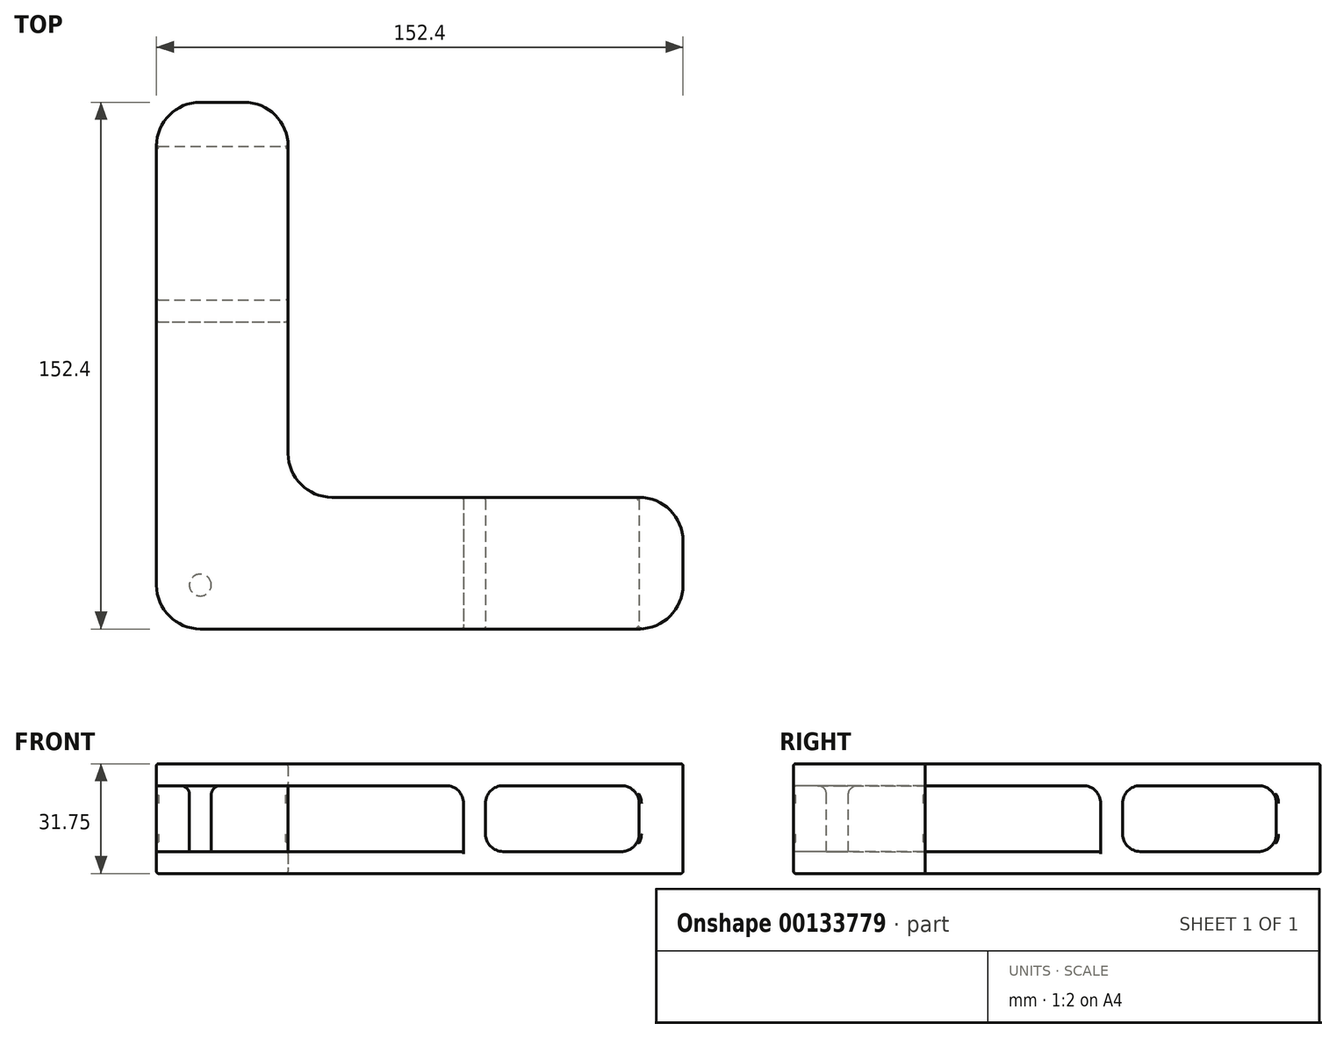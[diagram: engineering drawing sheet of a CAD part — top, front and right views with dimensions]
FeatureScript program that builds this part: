
annotation { "Feature Type Name" : "Feature", "Feature Type Description" : "" }
export const myFeature = defineFeature(function(context is Context, id is Id, definition is map)
    precondition{}
    {
        {
            var Q0;
            Q0=qCreatedBy(makeId("Top.planeOp"),FACE);
            var sketch = newSketch(context, id + "F0", { "sketchPlane" : qUnion([Q0])});
            skLineSegment(sketch, "E0", {"start": v(0, 12.7) * mm, "end": v(0, 139.7) * mm});
            skLineSegment(sketch, "E1", {"start": v(12.7, 152.4) * mm, "end": v(25.4, 152.4) * mm});
            skLineSegment(sketch, "E2", {"start": v(38.1, 139.7) * mm, "end": v(38.1, 50.8) * mm});
            skLineSegment(sketch, "E3", {"start": v(50.8, 38.1) * mm, "end": v(139.7, 38.1) * mm});
            skLineSegment(sketch, "E4", {"start": v(152.4, 25.4) * mm, "end": v(152.4, 12.7) * mm});
            skLineSegment(sketch, "E5", {"start": v(139.7, 0) * mm, "end": v(12.7, 0) * mm});
            skPoint(sketch, "E6.visualSharp", {"position": v(0, 0) * mm});
            skArc(sketch, "E6.filletArc", {"start": v(0, 12.7) * mm, "mid": v(3.72, 3.72) * mm, "end": v(12.7, 0) * mm});
            skPoint(sketch, "E7.visualSharp", {"position": v(0, 152.4) * mm});
            skArc(sketch, "E7.filletArc", {"start": v(12.7, 152.4) * mm, "mid": v(3.72, 148.68) * mm, "end": v(0, 139.7) * mm});
            skPoint(sketch, "E8.visualSharp", {"position": v(38.1, 152.4) * mm});
            skArc(sketch, "E8.filletArc", {"start": v(38.1, 139.7) * mm, "mid": v(34.38, 148.68) * mm, "end": v(25.4, 152.4) * mm});
            skPoint(sketch, "E9.visualSharp", {"position": v(38.1, 38.1) * mm});
            skArc(sketch, "E9.filletArc", {"start": v(38.1, 50.8) * mm, "mid": v(41.82, 41.82) * mm, "end": v(50.8, 38.1) * mm});
            skPoint(sketch, "E10.visualSharp", {"position": v(152.4, 38.1) * mm});
            skArc(sketch, "E10.filletArc", {"start": v(152.4, 25.4) * mm, "mid": v(148.68, 34.38) * mm, "end": v(139.7, 38.1) * mm});
            skPoint(sketch, "E11.visualSharp", {"position": v(152.4, 0) * mm});
            skArc(sketch, "E11.filletArc", {"start": v(139.7, 0) * mm, "mid": v(148.68, 3.72) * mm, "end": v(152.4, 12.7) * mm});
            skSolve(sketch);
        }
        {
            var Q0;
            Q0=makeQuery(id+"F0.imprint","IMPRINT",FACE,{"disambiguationData":[TD([[makeQuery(id+"F0.imprint","IMPRINT",EDGE,{"derivedFrom":sQuery(id+"F0.wireOp",EDGE,"E0")}),-1.0]])]});
            extrude(context, id + "F1", {"entities" : qUnion([Q0]), "depth" : 6.35 * mm});
        }
        {
            var Q0;
            Q0=makeQuery(id+"F1.opExtrude","CAP_FACE",FACE,{"disambiguationData":[OSD([sQuery(id+"F0.wireOp",EDGE,"E0"),sQuery(id+"F0.wireOp",EDGE,"E1"),sQuery(id+"F0.wireOp",EDGE,"E2"),sQuery(id+"F0.wireOp",EDGE,"E3"),sQuery(id+"F0.wireOp",EDGE,"E4"),sQuery(id+"F0.wireOp",EDGE,"E5"),sQuery(id+"F0.wireOp",EDGE,"E6.filletArc"),sQuery(id+"F0.wireOp",EDGE,"E7.filletArc"),sQuery(id+"F0.wireOp",EDGE,"E8.filletArc"),sQuery(id+"F0.wireOp",EDGE,"E9.filletArc"),sQuery(id+"F0.wireOp",EDGE,"E10.filletArc"),sQuery(id+"F0.wireOp",EDGE,"E11.filletArc")])],"isStart":false});
            extrude(context, id + "F2", {"entities" : qUnion([Q0]), "depth" : 6.35 * mm});
        }
        {
            var Q0;
            Q0=makeQuery(id+"F2.opExtrude","SWEPT_BODY",BODY,{"disambiguationData":[OSD([sQuery(id+"F0.wireOp",EDGE,"E0"),sQuery(id+"F0.wireOp",EDGE,"E1"),sQuery(id+"F0.wireOp",EDGE,"E2"),sQuery(id+"F0.wireOp",EDGE,"E3"),sQuery(id+"F0.wireOp",EDGE,"E4"),sQuery(id+"F0.wireOp",EDGE,"E5"),sQuery(id+"F0.wireOp",EDGE,"E6.filletArc"),sQuery(id+"F0.wireOp",EDGE,"E7.filletArc"),sQuery(id+"F0.wireOp",EDGE,"E8.filletArc"),sQuery(id+"F0.wireOp",EDGE,"E9.filletArc"),sQuery(id+"F0.wireOp",EDGE,"E10.filletArc"),sQuery(id+"F0.wireOp",EDGE,"E11.filletArc")])]});
            transform(context, id + "F3", {"entities" : qUnion([Q0]), "transformType" : TransformType.TRANSLATION_3D, "dx" : 0 * mm, "dy" : 0 * mm, "dz" : 19.05 * mm, "makeCopy" : false});
        }
        {
            var Q0;
            Q0=makeQuery(id+"F2.opExtrude","CAP_FACE",FACE,{"disambiguationData":[OSD([sQuery(id+"F0.wireOp",EDGE,"E0"),sQuery(id+"F0.wireOp",EDGE,"E1"),sQuery(id+"F0.wireOp",EDGE,"E2"),sQuery(id+"F0.wireOp",EDGE,"E3"),sQuery(id+"F0.wireOp",EDGE,"E4"),sQuery(id+"F0.wireOp",EDGE,"E5"),sQuery(id+"F0.wireOp",EDGE,"E6.filletArc"),sQuery(id+"F0.wireOp",EDGE,"E7.filletArc"),sQuery(id+"F0.wireOp",EDGE,"E8.filletArc"),sQuery(id+"F0.wireOp",EDGE,"E9.filletArc"),sQuery(id+"F0.wireOp",EDGE,"E10.filletArc"),sQuery(id+"F0.wireOp",EDGE,"E11.filletArc")])],"isStart":false});
            var sketch = newSketch(context, id + "F4", { "sketchPlane" : qUnion([Q0])});
            skArc(sketch, "E12.0", {"start": v(38.1, 139.7) * mm, "mid": v(34.38, 148.68) * mm, "end": v(25.4, 152.4) * mm});
            skLineSegment(sketch, "E13.0", {"start": v(12.7, 152.4) * mm, "end": v(25.4, 152.4) * mm});
            skArc(sketch, "E14.0", {"start": v(12.7, 152.4) * mm, "mid": v(3.72, 148.68) * mm, "end": v(0, 139.7) * mm});
            skArc(sketch, "E15.0", {"start": v(152.4, 25.4) * mm, "mid": v(148.68, 34.38) * mm, "end": v(139.7, 38.1) * mm});
            skLineSegment(sketch, "E16.0", {"start": v(152.4, 25.4) * mm, "end": v(152.4, 12.7) * mm});
            skArc(sketch, "E17.0", {"start": v(139.7, 0) * mm, "mid": v(148.68, 3.72) * mm, "end": v(152.4, 12.7) * mm});
            skLineSegment(sketch, "E18.0", {"start": v(50.8, 38.1) * mm, "end": v(139.7, 38.1) * mm});
            skLineSegment(sketch, "E19.0", {"start": v(139.7, 0) * mm, "end": v(12.7, 0) * mm});
            skLineSegment(sketch, "E20.0", {"start": v(38.1, 139.7) * mm, "end": v(38.1, 50.8) * mm});
            skLineSegment(sketch, "E21.0", {"start": v(0, 12.7) * mm, "end": v(0, 139.7) * mm});
            skArc(sketch, "E22.0", {"start": v(38.1, 50.8) * mm, "mid": v(41.82, 41.82) * mm, "end": v(50.8, 38.1) * mm});
            skArc(sketch, "E23.0", {"start": v(0, 12.7) * mm, "mid": v(3.72, 3.72) * mm, "end": v(12.7, 0) * mm});
            skLineSegment(sketch, "E24", {"start": v(0, 88.9) * mm, "end": v(38.1, 88.9) * mm});
            skLineSegment(sketch, "E25", {"start": v(88.9, 38.1) * mm, "end": v(88.9, 0) * mm});
            skLineSegment(sketch, "E26", {"start": v(95.25, 38.1) * mm, "end": v(95.25, 0) * mm});
            skLineSegment(sketch, "E27", {"start": v(0, 95.25) * mm, "end": v(38.1, 95.25) * mm});
            skLineSegment(sketch, "E28", {"start": v(0, 139.7) * mm, "end": v(38.1, 139.7) * mm});
            skLineSegment(sketch, "E29", {"start": v(139.7, 38.1) * mm, "end": v(139.7, 0) * mm});
            skSolve(sketch);
        }
        {
            var Q0;
            {var subQ0=sQuery(id+"F4.wireOp",EDGE,"E24");Q0=makeQuery(id+"F4.imprint","IMPRINT",FACE,{"disambiguationData":[TD([[makeQuery(id+"F4.imprint","IMPRINT",EDGE,{"derivedFrom":subQ0}),1.0]])]});}
            var Q1;
            Q1=makeQuery(id+"F4.imprint","IMPRINT",FACE,{"disambiguationData":[TD([[makeQuery(id+"F4.imprint","IMPRINT",EDGE,{"derivedFrom":sQuery(id+"F4.wireOp",EDGE,"E14.0")}),1.0]])]});
            var Q2;
            Q2=makeQuery(id+"F4.imprint","IMPRINT",FACE,{"disambiguationData":[TD([[makeQuery(id+"F4.imprint","IMPRINT",EDGE,{"derivedFrom":sQuery(id+"F4.wireOp",EDGE,"E15.0")}),1.0]])]});
            var Q3;
            {var subQ0=sQuery(id+"F4.wireOp",EDGE,"E25");Q3=makeQuery(id+"F4.imprint","IMPRINT",FACE,{"disambiguationData":[TD([[makeQuery(id+"F4.imprint","IMPRINT",EDGE,{"derivedFrom":subQ0}),1.0]])]});}
            extrude(context, id + "F5", {"entities" : qUnion([Q0, Q1, Q2, Q3]), "operationType" : NewBodyOperationType.ADD, "oppositeDirection" : true, "depth" : 25.4 * mm});
        }
        {
            var Q0;
            Q0=makeQuery(id+"F5.opExtrude","CAP_EDGE",EDGE,{"disambiguationData":[OSD([sQuery(id+"F4.wireOp",EDGE,"E28")])],"isStart":false});
            var Q1;
            Q1=makeQuery(id+"F5.boolean.opBoolean","INTERSECT",EDGE,{"derivedFrom":[makeQuery(id+"F2.opExtrude","CAP_FACE",FACE,{"disambiguationData":[OSD([sQuery(id+"F0.wireOp",EDGE,"E0"),sQuery(id+"F0.wireOp",EDGE,"E1"),sQuery(id+"F0.wireOp",EDGE,"E2"),sQuery(id+"F0.wireOp",EDGE,"E3"),sQuery(id+"F0.wireOp",EDGE,"E4"),sQuery(id+"F0.wireOp",EDGE,"E5"),sQuery(id+"F0.wireOp",EDGE,"E6.filletArc"),sQuery(id+"F0.wireOp",EDGE,"E7.filletArc"),sQuery(id+"F0.wireOp",EDGE,"E8.filletArc"),sQuery(id+"F0.wireOp",EDGE,"E9.filletArc"),sQuery(id+"F0.wireOp",EDGE,"E10.filletArc"),sQuery(id+"F0.wireOp",EDGE,"E11.filletArc")])],"isStart":true}),makeQuery(id+"F5.opExtrude","SWEPT_FACE",FACE,{"disambiguationData":[OSD([sQuery(id+"F4.wireOp",EDGE,"E28")])]})]});
            var Q2;
            Q2=makeQuery(id+"F5.boolean.opBoolean","INTERSECT",EDGE,{"derivedFrom":[makeQuery(id+"F2.opExtrude","CAP_FACE",FACE,{"disambiguationData":[OSD([sQuery(id+"F0.wireOp",EDGE,"E0"),sQuery(id+"F0.wireOp",EDGE,"E1"),sQuery(id+"F0.wireOp",EDGE,"E2"),sQuery(id+"F0.wireOp",EDGE,"E3"),sQuery(id+"F0.wireOp",EDGE,"E4"),sQuery(id+"F0.wireOp",EDGE,"E5"),sQuery(id+"F0.wireOp",EDGE,"E6.filletArc"),sQuery(id+"F0.wireOp",EDGE,"E7.filletArc"),sQuery(id+"F0.wireOp",EDGE,"E8.filletArc"),sQuery(id+"F0.wireOp",EDGE,"E9.filletArc"),sQuery(id+"F0.wireOp",EDGE,"E10.filletArc"),sQuery(id+"F0.wireOp",EDGE,"E11.filletArc")])],"isStart":true}),makeQuery(id+"F5.opExtrude","SWEPT_FACE",FACE,{"disambiguationData":[OSD([sQuery(id+"F4.wireOp",EDGE,"E27")])]})]});
            var Q3;
            Q3=makeQuery(id+"F5.opExtrude","CAP_EDGE",EDGE,{"disambiguationData":[OSD([sQuery(id+"F4.wireOp",EDGE,"E27")])],"isStart":false});
            var Q4;
            Q4=makeQuery(id+"F5.boolean.opBoolean","INTERSECT",EDGE,{"derivedFrom":[makeQuery(id+"F2.opExtrude","CAP_FACE",FACE,{"disambiguationData":[OSD([sQuery(id+"F0.wireOp",EDGE,"E0"),sQuery(id+"F0.wireOp",EDGE,"E1"),sQuery(id+"F0.wireOp",EDGE,"E2"),sQuery(id+"F0.wireOp",EDGE,"E3"),sQuery(id+"F0.wireOp",EDGE,"E4"),sQuery(id+"F0.wireOp",EDGE,"E5"),sQuery(id+"F0.wireOp",EDGE,"E6.filletArc"),sQuery(id+"F0.wireOp",EDGE,"E7.filletArc"),sQuery(id+"F0.wireOp",EDGE,"E8.filletArc"),sQuery(id+"F0.wireOp",EDGE,"E9.filletArc"),sQuery(id+"F0.wireOp",EDGE,"E10.filletArc"),sQuery(id+"F0.wireOp",EDGE,"E11.filletArc")])],"isStart":true}),makeQuery(id+"F5.opExtrude","SWEPT_FACE",FACE,{"disambiguationData":[OSD([sQuery(id+"F4.wireOp",EDGE,"E24")])]})]});
            var Q5;
            Q5=makeQuery(id+"F5.opExtrude","CAP_EDGE",EDGE,{"disambiguationData":[OSD([sQuery(id+"F4.wireOp",EDGE,"E24")])],"isStart":false});
            var Q6;
            Q6=makeQuery(id+"F5.opExtrude","CAP_EDGE",EDGE,{"disambiguationData":[OSD([sQuery(id+"F4.wireOp",EDGE,"E25")])],"isStart":false});
            var Q7;
            Q7=makeQuery(id+"F5.opExtrude","CAP_EDGE",EDGE,{"disambiguationData":[OSD([sQuery(id+"F4.wireOp",EDGE,"E29")])],"isStart":false});
            var Q8;
            Q8=makeQuery(id+"F5.boolean.opBoolean","INTERSECT",EDGE,{"derivedFrom":[makeQuery(id+"F2.opExtrude","CAP_FACE",FACE,{"disambiguationData":[OSD([sQuery(id+"F0.wireOp",EDGE,"E0"),sQuery(id+"F0.wireOp",EDGE,"E1"),sQuery(id+"F0.wireOp",EDGE,"E2"),sQuery(id+"F0.wireOp",EDGE,"E3"),sQuery(id+"F0.wireOp",EDGE,"E4"),sQuery(id+"F0.wireOp",EDGE,"E5"),sQuery(id+"F0.wireOp",EDGE,"E6.filletArc"),sQuery(id+"F0.wireOp",EDGE,"E7.filletArc"),sQuery(id+"F0.wireOp",EDGE,"E8.filletArc"),sQuery(id+"F0.wireOp",EDGE,"E9.filletArc"),sQuery(id+"F0.wireOp",EDGE,"E10.filletArc"),sQuery(id+"F0.wireOp",EDGE,"E11.filletArc")])],"isStart":true}),makeQuery(id+"F5.opExtrude","SWEPT_FACE",FACE,{"disambiguationData":[OSD([sQuery(id+"F4.wireOp",EDGE,"E25")])]})]});
            var Q9;
            Q9=makeQuery(id+"F5.boolean.opBoolean","INTERSECT",EDGE,{"derivedFrom":[makeQuery(id+"F2.opExtrude","CAP_FACE",FACE,{"disambiguationData":[OSD([sQuery(id+"F0.wireOp",EDGE,"E0"),sQuery(id+"F0.wireOp",EDGE,"E1"),sQuery(id+"F0.wireOp",EDGE,"E2"),sQuery(id+"F0.wireOp",EDGE,"E3"),sQuery(id+"F0.wireOp",EDGE,"E4"),sQuery(id+"F0.wireOp",EDGE,"E5"),sQuery(id+"F0.wireOp",EDGE,"E6.filletArc"),sQuery(id+"F0.wireOp",EDGE,"E7.filletArc"),sQuery(id+"F0.wireOp",EDGE,"E8.filletArc"),sQuery(id+"F0.wireOp",EDGE,"E9.filletArc"),sQuery(id+"F0.wireOp",EDGE,"E10.filletArc"),sQuery(id+"F0.wireOp",EDGE,"E11.filletArc")])],"isStart":true}),makeQuery(id+"F5.opExtrude","SWEPT_FACE",FACE,{"disambiguationData":[OSD([sQuery(id+"F4.wireOp",EDGE,"E29")])]})]});
            var Q10;
            Q10=makeQuery(id+"F5.boolean.opBoolean","INTERSECT",EDGE,{"derivedFrom":[makeQuery(id+"F2.opExtrude","CAP_FACE",FACE,{"disambiguationData":[OSD([sQuery(id+"F0.wireOp",EDGE,"E0"),sQuery(id+"F0.wireOp",EDGE,"E1"),sQuery(id+"F0.wireOp",EDGE,"E2"),sQuery(id+"F0.wireOp",EDGE,"E3"),sQuery(id+"F0.wireOp",EDGE,"E4"),sQuery(id+"F0.wireOp",EDGE,"E5"),sQuery(id+"F0.wireOp",EDGE,"E6.filletArc"),sQuery(id+"F0.wireOp",EDGE,"E7.filletArc"),sQuery(id+"F0.wireOp",EDGE,"E8.filletArc"),sQuery(id+"F0.wireOp",EDGE,"E9.filletArc"),sQuery(id+"F0.wireOp",EDGE,"E10.filletArc"),sQuery(id+"F0.wireOp",EDGE,"E11.filletArc")])],"isStart":true}),makeQuery(id+"F5.opExtrude","SWEPT_FACE",FACE,{"disambiguationData":[OSD([sQuery(id+"F4.wireOp",EDGE,"E26")])]})]});
            var Q11;
            Q11=makeQuery(id+"F5.opExtrude","CAP_EDGE",EDGE,{"disambiguationData":[OSD([sQuery(id+"F4.wireOp",EDGE,"E26")])],"isStart":false});
            fillet(context, id + "F6", {"entities" : qUnion([Q0, Q1, Q2, Q3, Q4, Q5, Q6, Q7, Q8, Q9, Q10, Q11]), "radius" : 5.08 * mm, "tangentPropagation" : true, "allowEdgeOverflow" : false});
        }
        {
            var Q0;
            Q0=makeQuery(id+"F2.opExtrude","CAP_EDGE",EDGE,{"disambiguationData":[OSD([sQuery(id+"F0.wireOp",EDGE,"E0")])],"isStart":false});
            var Q1;
            Q1=makeQuery(id+"F1.opExtrude","CAP_EDGE",EDGE,{"disambiguationData":[OSD([sQuery(id+"F0.wireOp",EDGE,"E0")])],"isStart":true});
            var Q2;
            {var subQ0=sQuery(id+"F0.wireOp",EDGE,"E0");var subQ1=sQuery(id+"F0.wireOp",EDGE,"E7.filletArc");Q2=makeQuery(id+"F5.boolean.opBoolean","SPLIT",EDGE,{"disambiguationData":[TD([makeQuery(id+"F1.opExtrude","SWEPT_FACE",FACE,{"disambiguationData":[OSD([subQ1])]})])],"derivedFrom":makeQuery(id+"F1.opExtrude","CAP_EDGE",EDGE,{"disambiguationData":[OSD([subQ0])],"isStart":false})});}
            var Q3;
            {var subQ0=sQuery(id+"F0.wireOp",EDGE,"E0");var subQ1=sQuery(id+"F0.wireOp",EDGE,"E6.filletArc");Q3=makeQuery(id+"F5.boolean.opBoolean","SPLIT",EDGE,{"disambiguationData":[TD([makeQuery(id+"F1.opExtrude","SWEPT_FACE",FACE,{"disambiguationData":[OSD([subQ1])]})])],"derivedFrom":makeQuery(id+"F1.opExtrude","CAP_EDGE",EDGE,{"disambiguationData":[OSD([subQ0])],"isStart":false})});}
            var Q4;
            {var subQ0=sQuery(id+"F0.wireOp",EDGE,"E2");var subQ1=sQuery(id+"F0.wireOp",EDGE,"E8.filletArc");Q4=makeQuery(id+"F5.boolean.opBoolean","SPLIT",EDGE,{"disambiguationData":[TD([makeQuery(id+"F1.opExtrude","SWEPT_FACE",FACE,{"disambiguationData":[OSD([subQ1])]})])],"derivedFrom":makeQuery(id+"F2.opExtrude","CAP_EDGE",EDGE,{"disambiguationData":[OSD([subQ0])],"isStart":true})});}
            var Q5;
            {var subQ0=sQuery(id+"F0.wireOp",EDGE,"E2");var subQ1=sQuery(id+"F0.wireOp",EDGE,"E9.filletArc");Q5=makeQuery(id+"F5.boolean.opBoolean","SPLIT",EDGE,{"disambiguationData":[TD([makeQuery(id+"F1.opExtrude","SWEPT_FACE",FACE,{"disambiguationData":[OSD([subQ1])]})])],"derivedFrom":makeQuery(id+"F1.opExtrude","CAP_EDGE",EDGE,{"disambiguationData":[OSD([subQ0])],"isStart":false})});}
            var Q6;
            {var subQ0=sQuery(id+"F0.wireOp",EDGE,"E3");var subQ1=sQuery(id+"F0.wireOp",EDGE,"E10.filletArc");Q6=makeQuery(id+"F5.boolean.opBoolean","SPLIT",EDGE,{"disambiguationData":[TD([makeQuery(id+"F1.opExtrude","SWEPT_FACE",FACE,{"disambiguationData":[OSD([subQ1])]})])],"derivedFrom":makeQuery(id+"F1.opExtrude","CAP_EDGE",EDGE,{"disambiguationData":[OSD([subQ0])],"isStart":false})});}
            var Q7;
            {var subQ0=sQuery(id+"F0.wireOp",EDGE,"E5");var subQ1=sQuery(id+"F0.wireOp",EDGE,"E11.filletArc");Q7=makeQuery(id+"F5.boolean.opBoolean","SPLIT",EDGE,{"disambiguationData":[TD([makeQuery(id+"F1.opExtrude","SWEPT_FACE",FACE,{"disambiguationData":[OSD([subQ1])]})])],"derivedFrom":makeQuery(id+"F1.opExtrude","CAP_EDGE",EDGE,{"disambiguationData":[OSD([subQ0])],"isStart":false})});}
            fillet(context, id + "F7", {"entities" : qUnion([Q0, Q1, Q2, Q3, Q4, Q5, Q6, Q7]), "radius" : 0.64 * mm, "tangentPropagation" : true, "allowEdgeOverflow" : false});
        }
        {
            var Q0;
            Q0=makeQuery(id+"F2.opExtrude","CAP_FACE",FACE,{"disambiguationData":[OSD([sQuery(id+"F0.wireOp",EDGE,"E0"),sQuery(id+"F0.wireOp",EDGE,"E1"),sQuery(id+"F0.wireOp",EDGE,"E2"),sQuery(id+"F0.wireOp",EDGE,"E3"),sQuery(id+"F0.wireOp",EDGE,"E4"),sQuery(id+"F0.wireOp",EDGE,"E5"),sQuery(id+"F0.wireOp",EDGE,"E6.filletArc"),sQuery(id+"F0.wireOp",EDGE,"E7.filletArc"),sQuery(id+"F0.wireOp",EDGE,"E8.filletArc"),sQuery(id+"F0.wireOp",EDGE,"E9.filletArc"),sQuery(id+"F0.wireOp",EDGE,"E10.filletArc"),sQuery(id+"F0.wireOp",EDGE,"E11.filletArc")])],"isStart":false});
            var sketch = newSketch(context, id + "F8", { "sketchPlane" : qUnion([Q0])});
            skCircle(sketch, "E30", {"center": v(12.7, 12.7) * mm, "radius": 3.18 * mm});
            skSolve(sketch);
        }
        {
            var Q0;
            Q0=makeQuery(id+"F8.imprint","IMPRINT",FACE,{"disambiguationData":[TD([[makeQuery(id+"F8.imprint","IMPRINT",EDGE,{"derivedFrom":sQuery(id+"F8.wireOp",EDGE,"E30")}),1.0]])]});
            extrude(context, id + "F9", {"entities" : qUnion([Q0]), "operationType" : NewBodyOperationType.ADD, "oppositeDirection" : true, "depth" : 25.4 * mm});
        }
        {
            var Q0;
            {var subQ0=sQuery(id+"F0.wireOp",EDGE,"E9.filletArc");var subQ1=sQuery(id+"F0.wireOp",EDGE,"E6.filletArc");var subQ2=sQuery(id+"F0.wireOp",EDGE,"E2");var subQ3=sQuery(id+"F0.wireOp",EDGE,"E5");var subQ4=sQuery(id+"F0.wireOp",EDGE,"E0");var subQ5=sQuery(id+"F0.wireOp",EDGE,"E3");Q0=makeQuery(id+"F9.boolean.opBoolean","INTERSECT",EDGE,{"derivedFrom":[makeQuery(id+"F5.boolean.opBoolean","SPLIT",FACE,{"disambiguationData":[TD([makeQuery(id+"F2.opExtrude","SWEPT_FACE",FACE,{"disambiguationData":[OSD([subQ1])]})])],"derivedFrom":makeQuery(id+"F2.opExtrude","CAP_FACE",FACE,{"disambiguationData":[OSD([subQ4,sQuery(id+"F0.wireOp",EDGE,"E1"),subQ2,subQ5,sQuery(id+"F0.wireOp",EDGE,"E4"),subQ3,subQ1,sQuery(id+"F0.wireOp",EDGE,"E7.filletArc"),sQuery(id+"F0.wireOp",EDGE,"E8.filletArc"),subQ0,sQuery(id+"F0.wireOp",EDGE,"E10.filletArc"),sQuery(id+"F0.wireOp",EDGE,"E11.filletArc")])],"isStart":true})}),makeQuery(id+"F9.opExtrude","SWEPT_FACE",FACE,{"disambiguationData":[OSD([sQuery(id+"F8.wireOp",EDGE,"E30")])]})]});}
            var Q1;
            Q1=makeQuery(id+"F9.opExtrude","CAP_EDGE",EDGE,{"disambiguationData":[OSD([sQuery(id+"F8.wireOp",EDGE,"E30")])],"isStart":false});
            fillet(context, id + "F10", {"entities" : qUnion([Q0, Q1]), "radius" : 2.54 * mm, "tangentPropagation" : true, "allowEdgeOverflow" : false});
        }
    });
